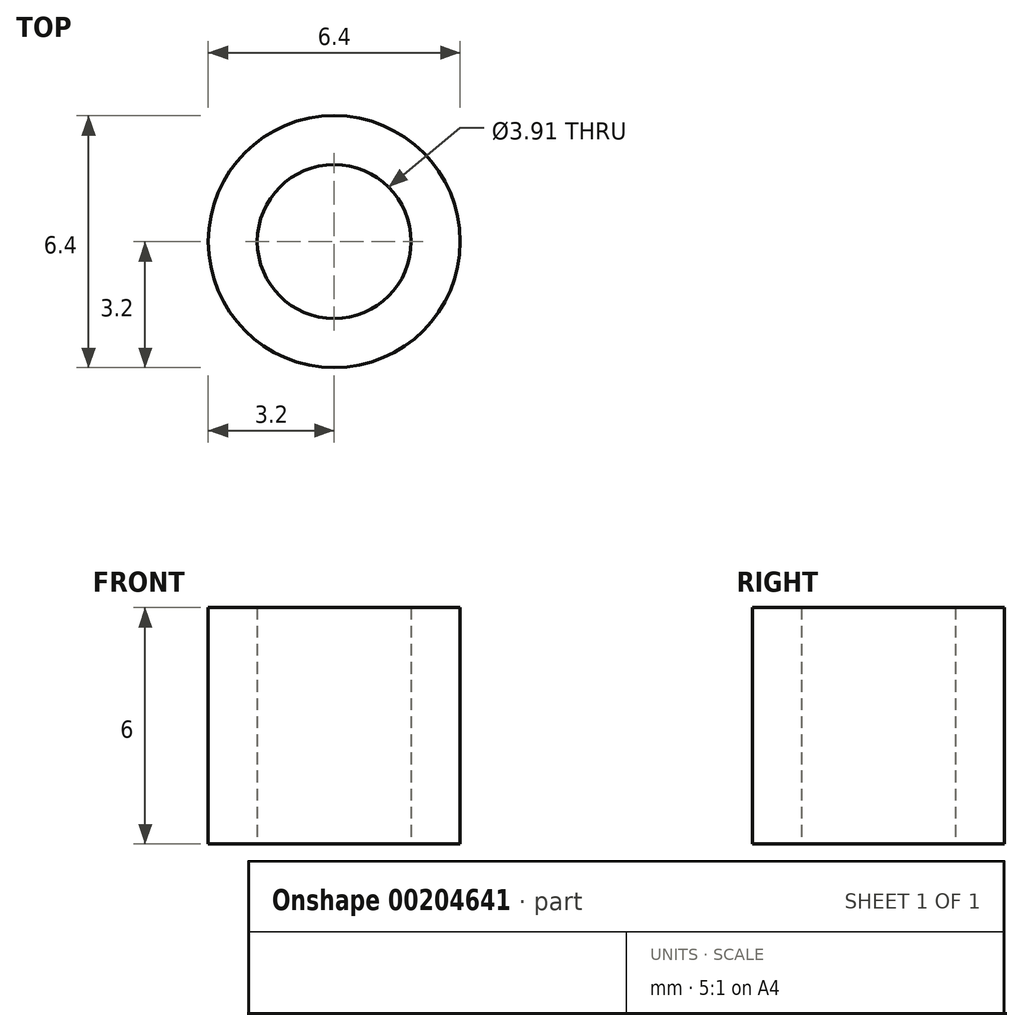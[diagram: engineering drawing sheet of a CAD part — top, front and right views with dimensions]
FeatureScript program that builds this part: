
annotation { "Feature Type Name" : "Feature", "Feature Type Description" : "" }
export const myFeature = defineFeature(function(context is Context, id is Id, definition is map)
    precondition{}
    {
        {
            var Q0;
            Q0=qCreatedBy(makeId("Top.planeOp"),FACE);
            var sketch = newSketch(context, id + "F0", { "sketchPlane" : qUnion([Q0])});
            skCircle(sketch, "E0", {"center": v(0, 0) * mm, "radius": 3.2 * mm});
            skCircle(sketch, "E1", {"center": v(0, 0) * mm, "radius": 1.96 * mm});
            skSolve(sketch);
        }
        {
            var Q0;
            Q0=makeQuery(id+"F0.imprint","IMPRINT",FACE,{"disambiguationData":[TD([[makeQuery(id+"F0.imprint","IMPRINT",EDGE,{"derivedFrom":sQuery(id+"F0.wireOp",EDGE,"E0")}),1.0]])]});
            extrude(context, id + "F1", {"entities" : qUnion([Q0]), "depth" : 6 * mm});
        }
    });
